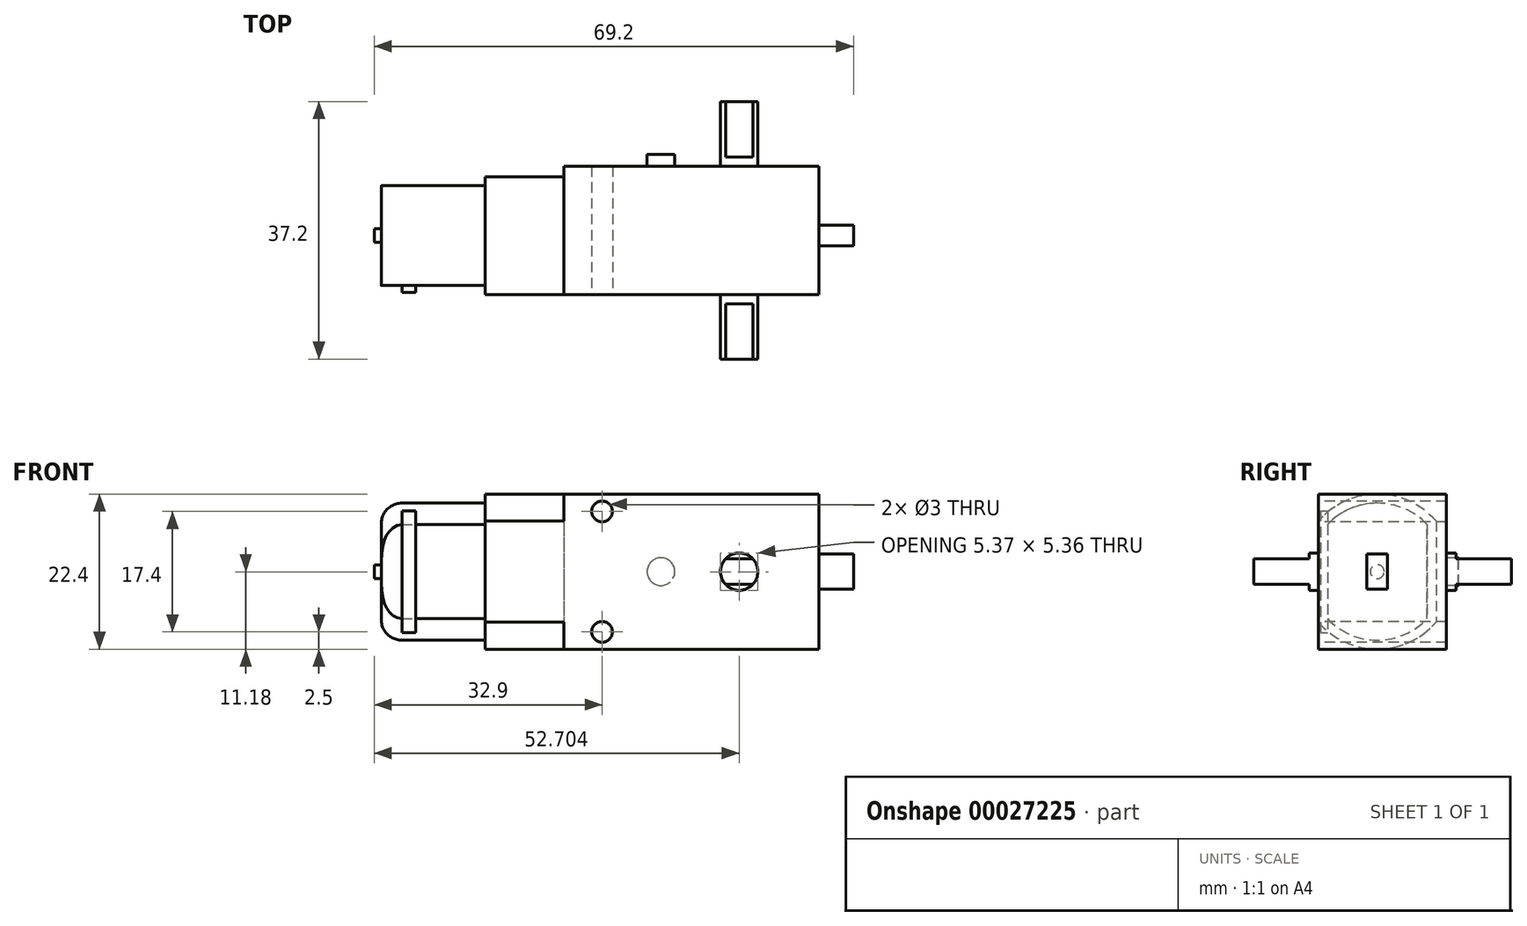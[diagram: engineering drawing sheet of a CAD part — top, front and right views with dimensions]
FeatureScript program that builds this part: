
annotation { "Feature Type Name" : "Feature", "Feature Type Description" : "" }
export const myFeature = defineFeature(function(context is Context, id is Id, definition is map)
    precondition{}
    {
        {
            var Q0;
            Q0=qCreatedBy(makeId("Top.planeOp"),FACE);
            var sketch = newSketch(context, id + "F0", { "sketchPlane" : qUnion([Q0])});
            skLineSegment(sketch, "E0.rect.bottom", {"start": v(18.4, 9.25) * mm, "end": v(-18.4, 9.25) * mm});
            skLineSegment(sketch, "E0.rect.top", {"start": v(18.4, -9.25) * mm, "end": v(-18.4, -9.25) * mm});
            skLineSegment(sketch, "E0.rect.left", {"start": v(18.4, 9.25) * mm, "end": v(18.4, -9.25) * mm});
            skLineSegment(sketch, "E0.rect.right", {"start": v(-18.4, 9.25) * mm, "end": v(-18.4, -9.25) * mm});
            skPoint(sketch, "E0.rect.middle", {"position": v(0, 0) * mm});
            skSolve(sketch);
        }
        {
            var Q0;
            Q0 = qSketchRegion(id + "F0", true);
            extrude(context, id + "F1", {"entities" : qUnion([Q0]), "depth" : 22.4 * mm});
        }
        {
            var Q0;
            Q0=makeQuery(id+"F1.opExtrude","SWEPT_FACE",FACE,{"disambiguationData":[OSD([sQuery(id+"F0.wireOp",EDGE,"E0.rect.left")])]});
            var sketch = newSketch(context, id + "F2", { "sketchPlane" : qUnion([Q0])});
            skLineSegment(sketch, "E1.rect.bottom", {"start": v(0.75, 13.75) * mm, "end": v(-2.25, 13.75) * mm});
            skLineSegment(sketch, "E1.rect.top", {"start": v(0.75, 8.65) * mm, "end": v(-2.25, 8.65) * mm});
            skLineSegment(sketch, "E1.rect.left", {"start": v(0.75, 13.75) * mm, "end": v(0.75, 8.65) * mm});
            skLineSegment(sketch, "E1.rect.right", {"start": v(-2.25, 13.75) * mm, "end": v(-2.25, 8.65) * mm});
            skPoint(sketch, "E1.rect.middle", {"position": v(-0.75, 11.2) * mm});
            skPoint(sketch, "E2", {"position": v(-9.25, 11.2) * mm});
            skSolve(sketch);
        }
        {
            var Q0;
            Q0 = qSketchRegion(id + "F2", true);
            extrude(context, id + "F3", {"entities" : qUnion([Q0]), "operationType" : NewBodyOperationType.ADD, "depth" : 5 * mm});
        }
        {
            var Q0;
            Q0=qCreatedBy(makeId("Front.planeOp"),FACE);
            var sketch = newSketch(context, id + "F4", { "sketchPlane" : qUnion([Q0])});
            skCircle(sketch, "E3", {"center": v(6.9, 11.2) * mm, "radius": 2.7 * mm});
            skLineSegment(sketch, "E4", {"start": v(0, 0) * mm, "end": v(0, 22.4) * mm, "construction": true});
            skPoint(sketch, "E5", {"position": v(0, 11.2) * mm});
            skSolve(sketch);
        }
        {
            var Q0;
            Q0 = qSketchRegion(id + "F4", true);
            extrude(context, id + "F5", {"entities" : qUnion([Q0]), "operationType" : NewBodyOperationType.ADD, "endBound" : BoundingType.SYMMETRIC, "depth" : 21.2 * mm});
        }
        {
            var Q0;
            Q0=makeQuery(id+"F5.opExtrude","CAP_FACE",FACE,{"disambiguationData":[OSD([sQuery(id+"F4.wireOp",EDGE,"E3")])],"isStart":false});
            var sketch = newSketch(context, id + "F6", { "sketchPlane" : qUnion([Q0])});
            skArc(sketch, "E6", {"start": v(4.93, 13.05) * mm, "mid": v(4.2, 11.2) * mm, "end": v(4.93, 9.35) * mm});
            skLineSegment(sketch, "E7.rect.bottom", {"start": v(4.93, 13.05) * mm, "end": v(8.87, 13.05) * mm});
            skLineSegment(sketch, "E7.rect.top", {"start": v(4.93, 9.35) * mm, "end": v(8.87, 9.35) * mm});
            skArc(sketch, "E8.trimOffspring", {"start": v(8.87, 9.35) * mm, "mid": v(9.6, 11.2) * mm, "end": v(8.87, 13.05) * mm});
            skSolve(sketch);
        }
        {
            var Q0;
            Q0 = qSketchRegion(id + "F6", true);
            extrude(context, id + "F7", {"entities" : qUnion([Q0]), "depth" : 8 * mm});
        }
        {
            var Q0;
            Q0=makeQuery(id+"F7.opExtrude","SWEPT_BODY",BODY,{"disambiguationData":[OSD([sQuery(id+"F6.wireOp",EDGE,"E6"),sQuery(id+"F6.wireOp",EDGE,"E7.rect.bottom"),sQuery(id+"F6.wireOp",EDGE,"E7.rect.top"),sQuery(id+"F6.wireOp",EDGE,"E8.trimOffspring")])]});
            var Q1;
            Q1=qCreatedBy(makeId("Front.planeOp"),FACE);
            mirror(context, id + "F8", {"operationType" : NewBodyOperationType.ADD, "entities" : qUnion([Q0]), "mirrorPlane" : qUnion([Q1])});
        }
        {
            var Q0;
            Q0=makeQuery(id+"F3.opExtrude","SWEPT_FACE",FACE,{"disambiguationData":[OSD([sQuery(id+"F2.wireOp",EDGE,"E1.rect.right")])]});
            var sketch = newSketch(context, id + "F9", { "sketchPlane" : qUnion([Q0])});
            skLineSegment(sketch, "E9", {"start": v(20.9, 13.75) * mm, "end": v(20.9, 8.65) * mm, "construction": true});
            skPoint(sketch, "E10", {"position": v(20.9, 11.2) * mm});
            skSolve(sketch);
        }
        {
            var Q0;
            Q0=makeQuery(id+"F1.opExtrude","SWEPT_FACE",FACE,{"disambiguationData":[OSD([sQuery(id+"F0.wireOp",EDGE,"E0.rect.bottom")])]});
            var sketch = newSketch(context, id + "F10", { "sketchPlane" : qUnion([Q0])});
            skCircle(sketch, "E11", {"center": v(4.4, 11.2) * mm, "radius": 2 * mm});
            skLineSegment(sketch, "E12", {"start": v(-18.4, 22.4) * mm, "end": v(-18.4, 0) * mm, "construction": true});
            skLineSegment(sketch, "E13", {"start": v(-18.4, 11.2) * mm, "end": v(18.4, 11.2) * mm, "construction": true});
            skSolve(sketch);
        }
        {
            var Q0;
            Q0 = qSketchRegion(id + "F10", true);
            extrude(context, id + "F11", {"entities" : qUnion([Q0]), "operationType" : NewBodyOperationType.ADD, "depth" : 1.7 * mm});
        }
        {
            var Q0;
            Q0=makeQuery(id+"F1.opExtrude","SWEPT_FACE",FACE,{"disambiguationData":[OSD([sQuery(id+"F0.wireOp",EDGE,"E0.rect.right")])]});
            var sketch = newSketch(context, id + "F12", { "sketchPlane" : qUnion([Q0])});
            skLineSegment(sketch, "E14", {"start": v(0.75, 22.4) * mm, "end": v(0.75, 0) * mm, "construction": true});
            skArc(sketch, "E15", {"start": v(-7.75, 3.9) * mm, "mid": v(0.75, 0) * mm, "end": v(9.25, 3.9) * mm});
            skLineSegment(sketch, "E16", {"start": v(9.25, 18.5) * mm, "end": v(9.25, 3.9) * mm});
            skLineSegment(sketch, "E17.MirrorCS", {"start": v(-7.75, 18.5) * mm, "end": v(-7.75, 3.9) * mm});
            skArc(sketch, "E18.trimOffspring", {"start": v(9.25, 18.5) * mm, "mid": v(0.75, 22.4) * mm, "end": v(-7.75, 18.5) * mm});
            skSolve(sketch);
        }
        {
            var Q0;
            Q0 = qSketchRegion(id + "F12", true);
            extrude(context, id + "F13", {"entities" : qUnion([Q0]), "operationType" : NewBodyOperationType.ADD, "depth" : 11.4 * mm});
        }
        {
            var Q0;
            Q0=makeQuery(id+"F13.opExtrude","CAP_FACE",FACE,{"disambiguationData":[OSD([sQuery(id+"F12.wireOp",EDGE,"E15"),sQuery(id+"F12.wireOp",EDGE,"E16"),sQuery(id+"F12.wireOp",EDGE,"E17.MirrorCS"),sQuery(id+"F12.wireOp",EDGE,"E18.trimOffspring")])],"isStart":false});
            var sketch = newSketch(context, id + "F14", { "sketchPlane" : qUnion([Q0])});
            skArc(sketch, "E19.0", {"start": v(7.95, 18) * mm, "mid": v(0.75, 21.1) * mm, "end": v(-6.45, 18) * mm});
            skLineSegment(sketch, "E19.1", {"start": v(7.95, 18) * mm, "end": v(7.95, 4.4) * mm});
            skArc(sketch, "E19.2", {"start": v(-6.45, 4.4) * mm, "mid": v(0.75, 1.3) * mm, "end": v(7.95, 4.4) * mm});
            skLineSegment(sketch, "E19.3", {"start": v(-6.45, 18) * mm, "end": v(-6.45, 4.4) * mm});
            skSolve(sketch);
        }
        {
            var Q0;
            Q0 = qSketchRegion(id + "F14", true);
            extrude(context, id + "F15", {"entities" : qUnion([Q0]), "operationType" : NewBodyOperationType.ADD, "depth" : 15 * mm});
        }
        {
            var Q0;
            Q0=makeQuery(id+"F15.opExtrude","CAP_EDGE",EDGE,{"disambiguationData":[OSD([sQuery(id+"F14.wireOp",EDGE,"E19.0")])],"isStart":false});
            fillet(context, id + "F16", {"entities" : qUnion([Q0]), "radius" : 3 * mm, "tangentPropagation" : true, "allowEdgeOverflow" : false});
        }
        {
            var Q0;
            Q0=makeQuery(id+"F15.opExtrude","CAP_FACE",FACE,{"disambiguationData":[OSD([sQuery(id+"F14.wireOp",EDGE,"E19.0"),sQuery(id+"F14.wireOp",EDGE,"E19.1"),sQuery(id+"F14.wireOp",EDGE,"E19.2"),sQuery(id+"F14.wireOp",EDGE,"E19.3")])],"isStart":false});
            var sketch = newSketch(context, id + "F17", { "sketchPlane" : qUnion([Q0])});
            skCircle(sketch, "E20", {"center": v(0.75, 11.2) * mm, "radius": 1 * mm});
            skSolve(sketch);
        }
        {
            var Q0;
            Q0 = qSketchRegion(id + "F17", true);
            extrude(context, id + "F18", {"entities" : qUnion([Q0]), "operationType" : NewBodyOperationType.ADD, "depth" : 1 * mm});
        }
        {
            var Q0;
            Q0=makeQuery(id+"F15.opExtrude","SWEPT_FACE",FACE,{"disambiguationData":[OSD([sQuery(id+"F14.wireOp",EDGE,"E19.1")])]});
            var sketch = newSketch(context, id + "F19", { "sketchPlane" : qUnion([Q0])});
            skLineSegment(sketch, "E21.bottom", {"start": v(-39.8, 20) * mm, "end": v(-41.8, 20) * mm});
            skLineSegment(sketch, "E21.left", {"start": v(-39.8, 20) * mm, "end": v(-39.8, 2.4) * mm});
            skLineSegment(sketch, "E21.right", {"start": v(-41.8, 20) * mm, "end": v(-41.8, 2.4) * mm});
            skLineSegment(sketch, "E22", {"start": v(-39.8, 2.4) * mm, "end": v(-41.8, 2.4) * mm});
            skSolve(sketch);
        }
        {
            var Q0;
            Q0 = qSketchRegion(id + "F19", true);
            extrude(context, id + "F20", {"entities" : qUnion([Q0]), "operationType" : NewBodyOperationType.ADD, "depth" : 1 * mm});
        }
        {
            var Q0;
            Q0=makeQuery(id+"F13.boolean.opBoolean","MERGE",FACE,{"derivedFrom":[makeQuery(id+"F1.opExtrude","SWEPT_FACE",FACE,{"disambiguationData":[OSD([sQuery(id+"F0.wireOp",EDGE,"E0.rect.top")])]}),makeQuery(id+"F13.opExtrude","SWEPT_FACE",FACE,{"disambiguationData":[OSD([sQuery(id+"F12.wireOp",EDGE,"E16")])]})]});
            var sketch = newSketch(context, id + "F21", { "sketchPlane" : qUnion([Q0])});
            skCircle(sketch, "E23", {"center": v(-12.9, 19.9) * mm, "radius": 1.5 * mm});
            skLineSegment(sketch, "E24", {"start": v(-29.8, 11.2) * mm, "end": v(18.4, 11.2) * mm, "construction": true});
            skCircle(sketch, "E25.MirrorC", {"center": v(-12.9, 2.5) * mm, "radius": 1.5 * mm});
            skSolve(sketch);
        }
        {
            var Q0;
            Q0 = qSketchRegion(id + "F21", true);
            extrude(context, id + "F22", {"entities" : qUnion([Q0]), "operationType" : NewBodyOperationType.REMOVE, "endBound" : BoundingType.THROUGH_ALL, "oppositeDirection" : true, "depth" : 25 * mm});
        }
    });
